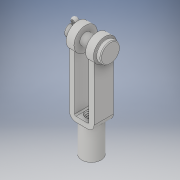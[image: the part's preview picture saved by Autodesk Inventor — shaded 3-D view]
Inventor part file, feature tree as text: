
AUTODESK INVENTOR PART (.ipt)
format: ipt  version: 2018 (Build 220112000, 112)  size: 653,312 bytes
history: native  units: in
note: dims shown in document units (in); Inventor stores cm internally (conversion verified against a paired STEP export)
features: extrude x2, other x1
ambient origin geometry x8: Origin, YZ Plane, XZ Plane, XY Plane, X Axis, Y Axis, Z Axis, Center Point
bodies: Solid1 (feature_tree), Solid2 (feature_tree), Solid3 (feature_tree)
feature tree (3):
  other  "Cut-Extrude5"
  extrude  "Extrude3"  [1 undecoded]
  extrude  "Extrude6"  [1 undecoded]
note: 2 required parameter values undecoded (feature->parameter linkage not recoverable at this tier; creation-order binding heuristic only, values carry confidence <= 0.55)
